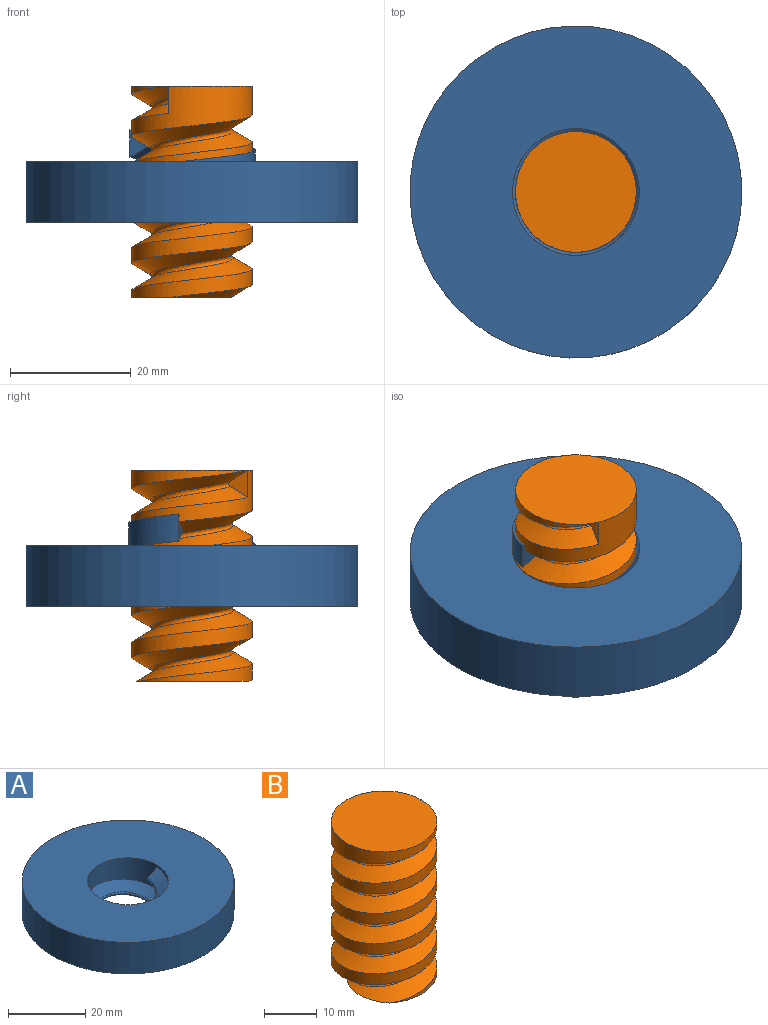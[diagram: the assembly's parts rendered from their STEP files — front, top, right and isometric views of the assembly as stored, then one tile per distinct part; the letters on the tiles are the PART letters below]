
ASSEMBLY  parts=2 mates=1
PART A: 11 faces, bbox 55x55x15.8 mm
  f0: cylinder r=10.5mm len=21mm, axis (0,0,-1), area 280.4mm2, adj f1,f3,f6,f8
  f1: cylinder r=10.5mm len=21mm, axis (0,0,-1), area 82.7mm2, adj f0,f4,f8,f10
  f2: cylinder r=27.5mm len=55mm, axis (0,0,-1), area 1727.9mm2, adj f3,f4
  f3: plane 55x55mm, normal (0,0,1), area 2029.5mm2, adj f0,f2
  f4: plane 55x55mm, normal (0,0,-1), area 2029.5mm2, adj f1,f2,f5
  f5: cylinder r=10.5mm len=21mm, axis (0,0,-1), area 127mm2, adj f4,f7,f8,f10
  f6: plane 4.54x3.44mm, normal (0,1,0), area 8.6mm2, adj f0,f8,f9,f10
  f7: plane 4.54x3.1mm, normal (-0.43,0.9,0), area 8.6mm2, adj f5,f8,f9,f10
  f8: bspline ~24.25x21mm, area 292.8mm2, adj f0,f1,f5,f6,f7,f9
  f9: bspline ~16.98x14.71mm, area 67.8mm2, adj f6,f7,f8,f10
  f10: bspline ~24.25x21mm, area 292.9mm2, adj f1,f5,f6,f7,f9
PART B: 7 faces, bbox 20.2x23.3x37.3 mm
  f0: cylinder r=10mm len=35mm, axis (0,0,-1), area 864.3mm2, adj f1,f2,f3,f5,f6
  f1: plane 20x20mm, normal (0,0,1), area 314.2mm2, adj f0
  f2: plane 18.64x17.42mm, normal (0,0,-1), area 246.7mm2, adj f0,f3,f4,f5
  f3: bspline ~34.48x23.09mm, area 867mm2, adj f0,f2,f4,f6
  f4: bspline ~34.7x15.83mm, area 206.7mm2, adj f2,f3,f5,f6
  f5: bspline ~36.82x23.09mm, area 944mm2, adj f0,f2,f4,f6
  f6: plane 4.54x3.44mm, normal (0,-1,0), area 8.6mm2, adj f0,f3,f4,f5
PLACE A rot(axis=(0.99,0.12,0),180deg) t=(3.38,27.34,16.01)mm fixed
PLACE B rot(axis=(0,0,-1),113.1deg) t=(3.38,27.34,-6.5)mm
MATE cylindrical B.f0 <-> A.f0  axis (0,0,-1) through (3.38,27.34,11)mm
